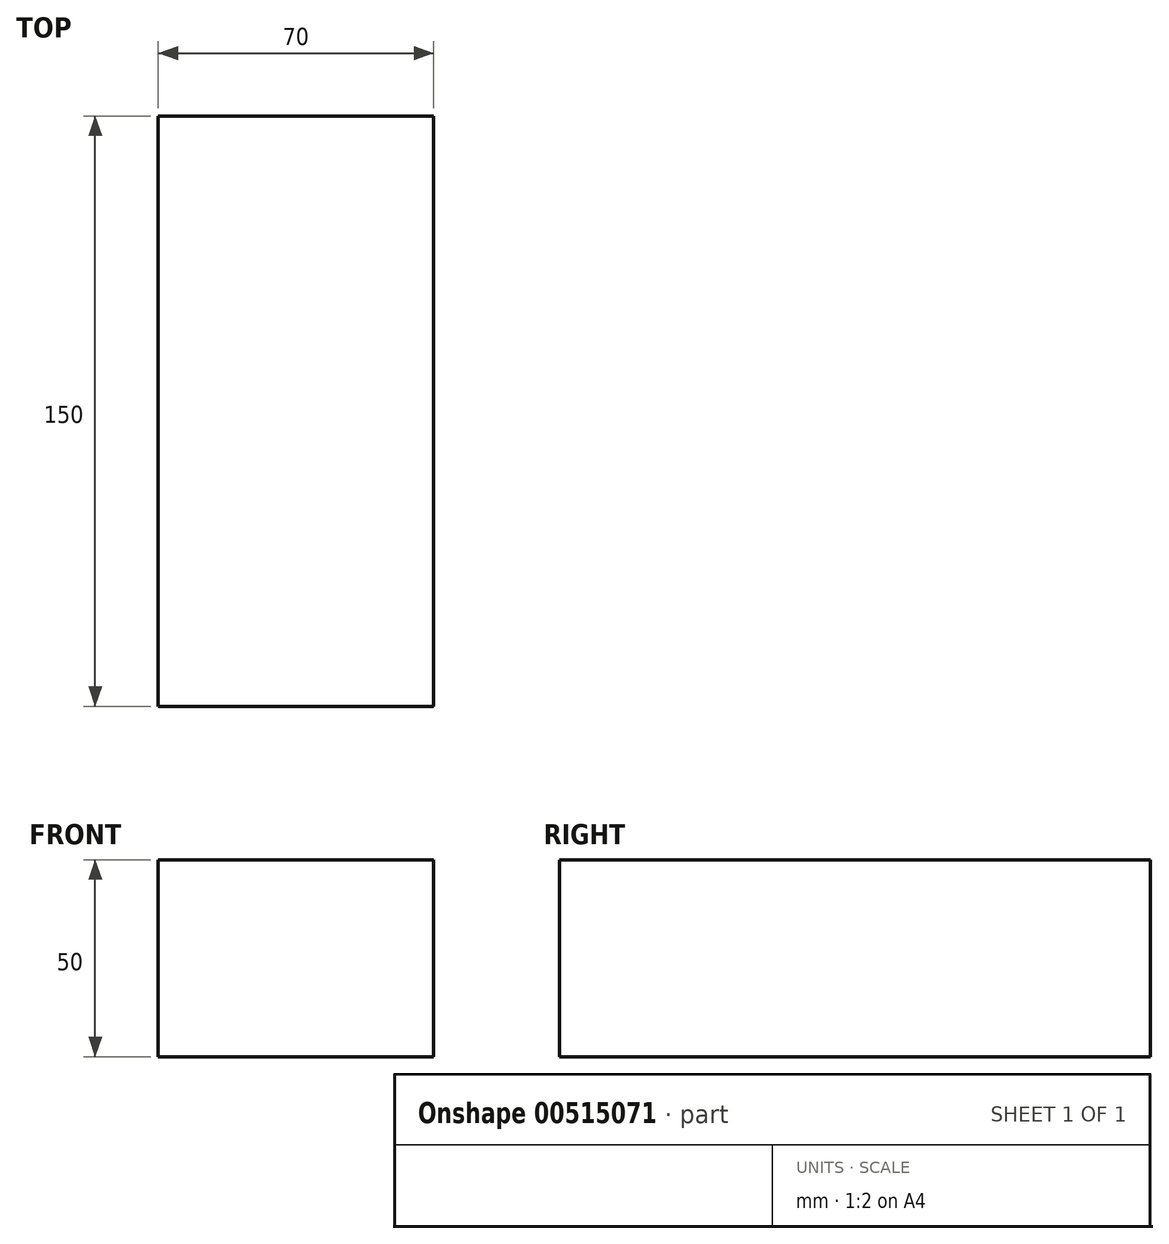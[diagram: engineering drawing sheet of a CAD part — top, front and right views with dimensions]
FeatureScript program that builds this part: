
annotation { "Feature Type Name" : "Feature", "Feature Type Description" : "" }
export const myFeature = defineFeature(function(context is Context, id is Id, definition is map)
    precondition{}
    {
        {
            var Q0;
            Q0=qCreatedBy(makeId("Front.planeOp"),FACE);
            var sketch = newSketch(context, id + "F0", { "sketchPlane" : qUnion([Q0])});
            skLineSegment(sketch, "E0.bottom", {"start": v(-35.5, 17.95) * mm, "end": v(34.5, 17.95) * mm});
            skLineSegment(sketch, "E0.top", {"start": v(-35.5, -32.05) * mm, "end": v(34.5, -32.05) * mm});
            skLineSegment(sketch, "E0.left", {"start": v(-35.5, 17.95) * mm, "end": v(-35.5, -32.05) * mm});
            skLineSegment(sketch, "E0.right", {"start": v(34.5, 17.95) * mm, "end": v(34.5, -32.05) * mm});
            skSolve(sketch);
        }
        {
            var Q0;
            Q0=makeQuery(id+"F0.imprint","IMPRINT",FACE,{"disambiguationData":[TD([[makeQuery(id+"F0.imprint","IMPRINT",EDGE,{"derivedFrom":sQuery(id+"F0.wireOp",EDGE,"E0.bottom")}),-1.0]])]});
            extrude(context, id + "F1", {"entities" : qUnion([Q0]), "depth" : 150 * mm, "offsetDistance" : 25 * mm});
        }
    });
